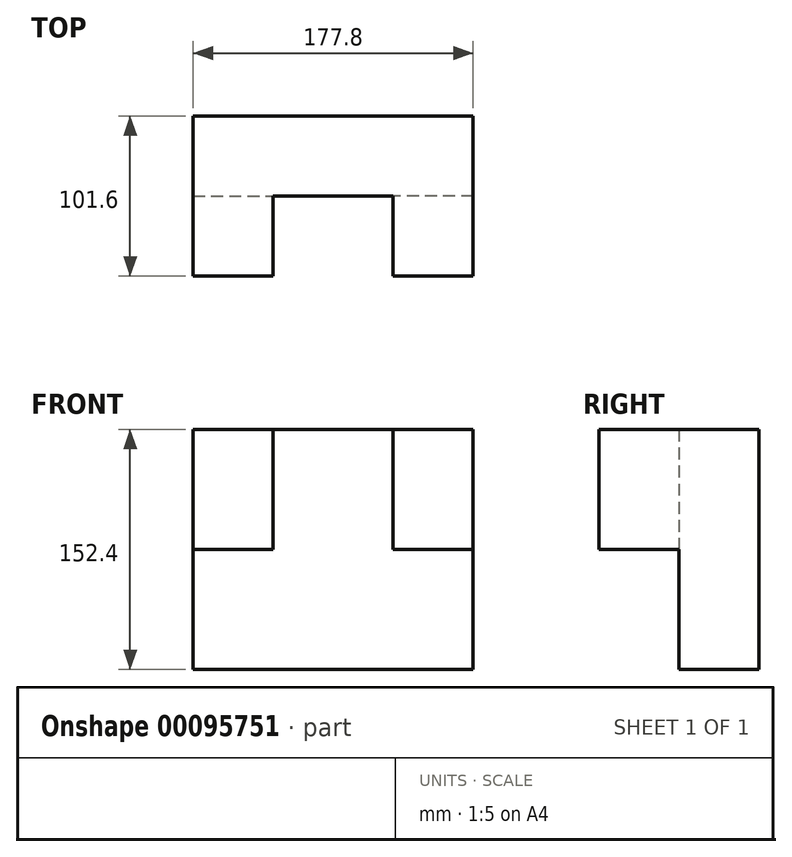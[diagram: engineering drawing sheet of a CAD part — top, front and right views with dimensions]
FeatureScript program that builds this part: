
annotation { "Feature Type Name" : "Feature", "Feature Type Description" : "" }
export const myFeature = defineFeature(function(context is Context, id is Id, definition is map)
    precondition{}
    {
        {
            var Q0;
            Q0=qCreatedBy(makeId("Front.planeOp"),FACE);
            var sketch = newSketch(context, id + "F0", { "sketchPlane" : qUnion([Q0])});
            skLineSegment(sketch, "E0", {"start": v(-86.9, -72.77) * mm, "end": v(90.9, -72.77) * mm});
            skLineSegment(sketch, "E1", {"start": v(90.9, -72.77) * mm, "end": v(90.9, 79.63) * mm});
            skLineSegment(sketch, "E2", {"start": v(90.9, 79.63) * mm, "end": v(-86.9, 79.63) * mm});
            skLineSegment(sketch, "E3", {"start": v(-86.9, 79.63) * mm, "end": v(-86.9, -72.77) * mm});
            skSolve(sketch);
        }
        {
            var Q0;
            Q0 = qSketchRegion(id + "F0", true);
            extrude(context, id + "F1", {"entities" : qUnion([Q0]), "depth" : 50.8 * mm});
        }
        {
            var Q0;
            Q0=makeQuery(id+"F1.opExtrude","CAP_FACE",FACE,{"disambiguationData":[OSD([sQuery(id+"F0.wireOp",EDGE,"E0"),sQuery(id+"F0.wireOp",EDGE,"E1"),sQuery(id+"F0.wireOp",EDGE,"E2"),sQuery(id+"F0.wireOp",EDGE,"E3")])],"isStart":false});
            var sketch = newSketch(context, id + "F2", { "sketchPlane" : qUnion([Q0])});
            skLineSegment(sketch, "E4.bottom", {"start": v(-86.9, 79.63) * mm, "end": v(-36.1, 79.63) * mm});
            skLineSegment(sketch, "E4.top", {"start": v(-86.9, 3.43) * mm, "end": v(-36.1, 3.43) * mm});
            skLineSegment(sketch, "E4.left", {"start": v(-86.9, 79.63) * mm, "end": v(-86.9, 3.43) * mm});
            skLineSegment(sketch, "E4.right", {"start": v(-36.1, 79.63) * mm, "end": v(-36.1, 3.43) * mm});
            skLineSegment(sketch, "E5.bottom", {"start": v(90.9, 79.63) * mm, "end": v(40.1, 79.63) * mm});
            skLineSegment(sketch, "E5.top", {"start": v(90.9, 3.43) * mm, "end": v(40.1, 3.43) * mm});
            skLineSegment(sketch, "E5.left", {"start": v(90.9, 79.63) * mm, "end": v(90.9, 3.43) * mm});
            skLineSegment(sketch, "E5.right", {"start": v(40.1, 79.63) * mm, "end": v(40.1, 3.43) * mm});
            skSolve(sketch);
        }
        {
            var Q0;
            Q0 = qSketchRegion(id + "F2", true);
            extrude(context, id + "F3", {"entities" : qUnion([Q0]), "operationType" : NewBodyOperationType.ADD, "depth" : 50.8 * mm});
        }
    });
